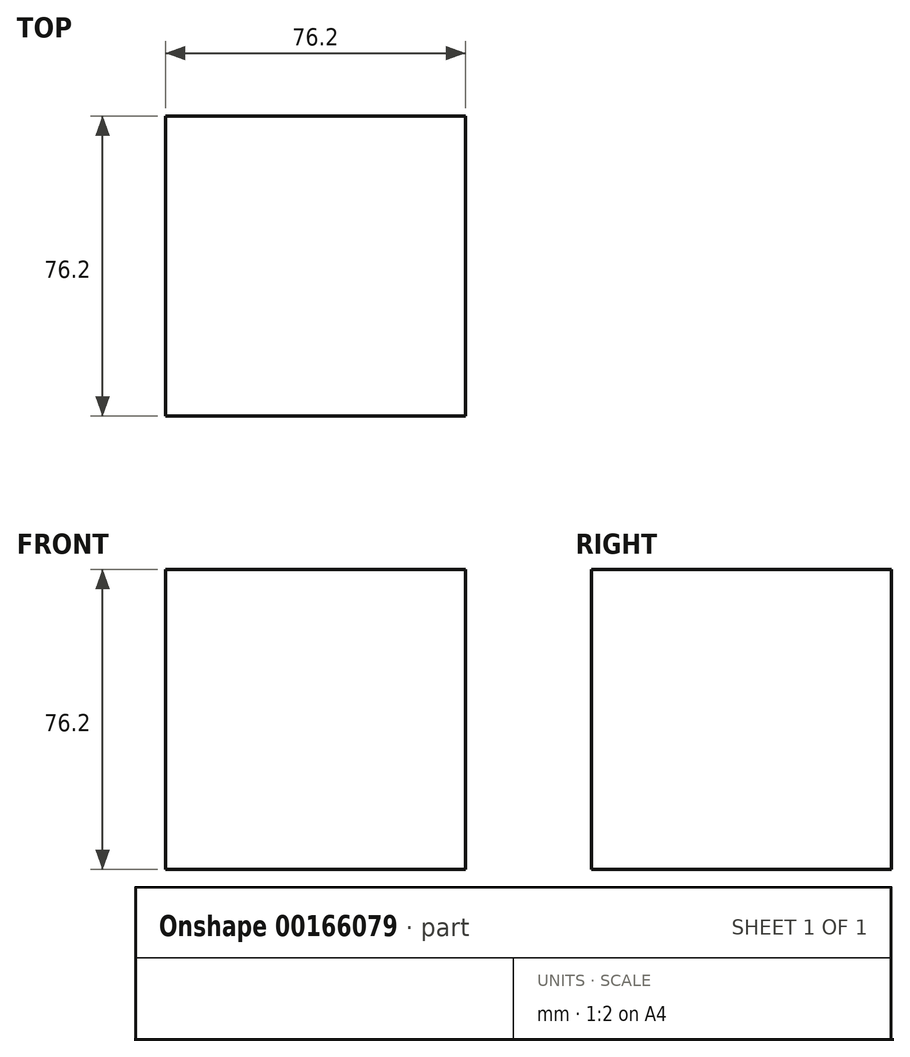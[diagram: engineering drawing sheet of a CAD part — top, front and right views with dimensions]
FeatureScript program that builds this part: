
annotation { "Feature Type Name" : "Feature", "Feature Type Description" : "" }
export const myFeature = defineFeature(function(context is Context, id is Id, definition is map)
    precondition{}
    {
        {
            var Q0;
            Q0=qCreatedBy(makeId("Front.planeOp"),FACE);
            var sketch = newSketch(context, id + "F0", { "sketchPlane" : qUnion([Q0])});
            skLineSegment(sketch, "E0.bottom", {"start": v(38.1, 38.1) * mm, "end": v(-38.1, 38.1) * mm});
            skLineSegment(sketch, "E0.top", {"start": v(38.1, -38.1) * mm, "end": v(-38.1, -38.1) * mm});
            skLineSegment(sketch, "E0.left", {"start": v(38.1, 38.1) * mm, "end": v(38.1, -38.1) * mm});
            skLineSegment(sketch, "E0.right", {"start": v(-38.1, 38.1) * mm, "end": v(-38.1, -38.1) * mm});
            skPoint(sketch, "E0.middle", {"position": v(0, 0) * mm});
            skSolve(sketch);
        }
        {
            var Q0;
            Q0=makeQuery(id+"F0.imprint","IMPRINT",FACE,{"disambiguationData":[TD([[makeQuery(id+"F0.imprint","IMPRINT",EDGE,{"derivedFrom":sQuery(id+"F0.wireOp",EDGE,"E0.bottom")}),1.0]])]});
            extrude(context, id + "F1", {"entities" : qUnion([Q0]), "oppositeDirection" : true, "depth" : 76.2 * mm});
        }
    });
